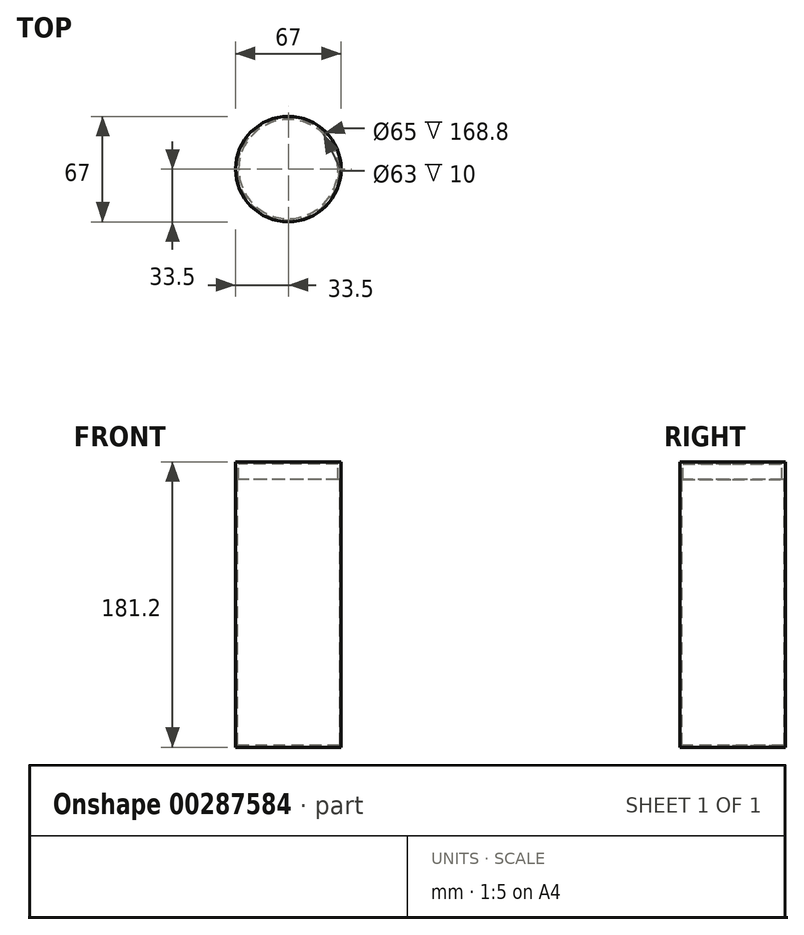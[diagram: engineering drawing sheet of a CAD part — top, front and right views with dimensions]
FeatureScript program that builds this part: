
annotation { "Feature Type Name" : "Feature", "Feature Type Description" : "" }
export const myFeature = defineFeature(function(context is Context, id is Id, definition is map)
    precondition{}
    {
        {
            var Q0;
            Q0=qCreatedBy(makeId("Top.planeOp"),FACE);
            var sketch = newSketch(context, id + "F0", { "sketchPlane" : qUnion([Q0])});
            skCircle(sketch, "E0", {"center": v(0, 0) * mm, "radius": 32.5 * mm});
            skCircle(sketch, "E1", {"center": v(0, 0) * mm, "radius": 33.5 * mm});
            skSolve(sketch);
        }
        {
            var Q0;
            Q0 = qSketchRegion(id + "F0", true);
            extrude(context, id + "F1", {"entities" : qUnion([Q0]), "depth" : 180 * mm, "offsetDistance" : 25 * mm});
        }
        {
            var Q0;
            Q0=makeQuery(id+"F0.imprint","IMPRINT",FACE,{"disambiguationData":[TD([[makeQuery(id+"F0.imprint","IMPRINT",EDGE,{"derivedFrom":sQuery(id+"F0.wireOp",EDGE,"E0")}),1.0]])]});
            extrude(context, id + "F2", {"entities" : qUnion([Q0]), "operationType" : NewBodyOperationType.ADD, "depth" : 1.2 * mm, "offsetDistance" : 25 * mm});
        }
        {
            var Q0;
            Q0=makeQuery(id+"F1.opExtrude","CAP_FACE",FACE,{"disambiguationData":[OSD([sQuery(id+"F0.wireOp",EDGE,"E0"),sQuery(id+"F0.wireOp",EDGE,"E1")])],"isStart":false});
            var sketch = newSketch(context, id + "F3", { "sketchPlane" : qUnion([Q0])});
            skCircle(sketch, "E2", {"center": v(0, 0) * mm, "radius": 32.5 * mm});
            skCircle(sketch, "E3", {"center": v(0, 0) * mm, "radius": 33.5 * mm});
            skCircle(sketch, "E4", {"center": v(0, 0) * mm, "radius": 31.5 * mm});
            skSolve(sketch);
        }
        {
            var Q0;
            Q0 = qSketchRegion(id + "F3", true);
            var Q1;
            Q1=makeQuery(id+"F3.imprint","IMPRINT",FACE,{"disambiguationData":[TD([[makeQuery(id+"F3.imprint","IMPRINT",EDGE,{"derivedFrom":sQuery(id+"F3.wireOp",EDGE,"E2")}),1.0]])]});
            var Q2;
            Q2=makeQuery(id+"F3.imprint","IMPRINT",FACE,{"disambiguationData":[TD([[makeQuery(id+"F3.imprint","IMPRINT",EDGE,{"derivedFrom":sQuery(id+"F3.wireOp",EDGE,"E4")}),1.0]])]});
            extrude(context, id + "F4", {"entities" : qUnion([Q0, Q1, Q2]), "depth" : 1.2 * mm, "offsetDistance" : 25 * mm});
        }
        {
            var Q0;
            Q0=makeQuery(id+"F3.imprint","IMPRINT",FACE,{"disambiguationData":[TD([[makeQuery(id+"F3.imprint","IMPRINT",EDGE,{"derivedFrom":sQuery(id+"F3.wireOp",EDGE,"E2")}),1.0]])]});
            extrude(context, id + "F5", {"entities" : qUnion([Q0]), "operationType" : NewBodyOperationType.ADD, "oppositeDirection" : true, "depth" : 10 * mm, "offsetDistance" : 25 * mm});
        }
    });
